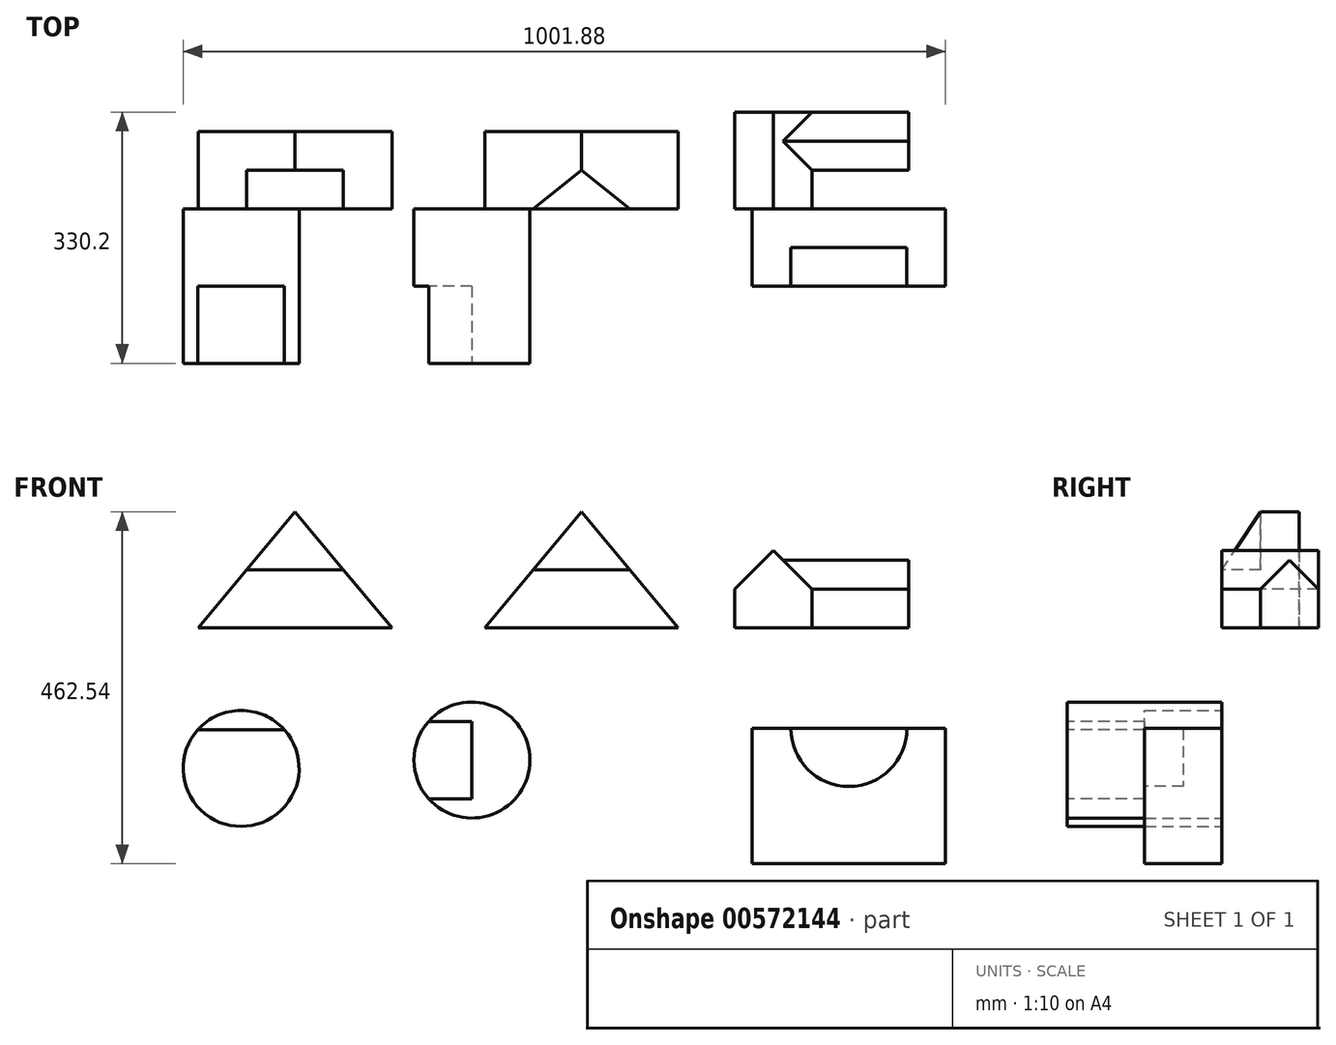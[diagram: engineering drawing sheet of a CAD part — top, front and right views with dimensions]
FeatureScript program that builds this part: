
annotation { "Feature Type Name" : "Feature", "Feature Type Description" : "" }
export const myFeature = defineFeature(function(context is Context, id is Id, definition is map)
    precondition{}
    {
        {
            var Q0;
            Q0=qCreatedBy(makeId("Front.planeOp"),FACE);
            var sketch = newSketch(context, id + "F0", { "sketchPlane" : qUnion([Q0])});
            skLineSegment(sketch, "E0.bottom", {"start": v(148.7, 0) * mm, "end": v(403.3, 0) * mm});
            skLineSegment(sketch, "E1", {"start": v(276, 152.77) * mm, "end": v(403.3, 0) * mm});
            skLineSegment(sketch, "E2", {"start": v(148.7, 0) * mm, "end": v(276, 152.77) * mm});
            skLineSegment(sketch, "E3", {"start": v(212.34, 76.38) * mm, "end": v(339.65, 76.38) * mm});
            skLineSegment(sketch, "E4.bottom", {"start": v(525.25, 0) * mm, "end": v(779.25, 0) * mm});
            skLineSegment(sketch, "E5", {"start": v(525.25, 0) * mm, "end": v(652.25, 152.4) * mm});
            skLineSegment(sketch, "E6", {"start": v(652.25, 152.4) * mm, "end": v(779.25, 0) * mm});
            skLineSegment(sketch, "E7", {"start": v(588.75, 76.2) * mm, "end": v(715.75, 76.2) * mm});
            skSolve(sketch);
        }
        {
            var Q0;
            {var subQ3=sQuery(id+"F0.wireOp",EDGE,"E3");Q0=makeQuery(id+"F0.imprint","IMPRINT",FACE,{"disambiguationData":[TD([[makeQuery(id+"F0.imprint","IMPRINT",EDGE,{"derivedFrom":subQ3}),1.0]])]});}
            var Q1;
            {var subQ0=sQuery(id+"F0.wireOp",EDGE,"E0.bottom");Q1=makeQuery(id+"F0.imprint","IMPRINT",FACE,{"disambiguationData":[TD([[makeQuery(id+"F0.imprint","IMPRINT",EDGE,{"derivedFrom":subQ0}),1.0]])]});}
            extrude(context, id + "F1", {"entities" : qUnion([Q0, Q1]), "oppositeDirection" : true, "depth" : 101.6 * mm, "offsetDistance" : 25.4 * mm});
        }
        {
            var Q0;
            {var subQ3=sQuery(id+"F0.wireOp",EDGE,"E3");Q0=makeQuery(id+"F0.imprint","IMPRINT",FACE,{"disambiguationData":[TD([[makeQuery(id+"F0.imprint","IMPRINT",EDGE,{"derivedFrom":subQ3}),1.0]])]});}
            extrude(context, id + "F2", {"entities" : qUnion([Q0]), "operationType" : NewBodyOperationType.REMOVE, "oppositeDirection" : true, "depth" : 50.8 * mm, "offsetDistance" : 25.4 * mm});
        }
        {
            var Q0;
            {var subQ3=sQuery(id+"F0.wireOp",EDGE,"E7");Q0=makeQuery(id+"F0.imprint","IMPRINT",FACE,{"disambiguationData":[TD([[makeQuery(id+"F0.imprint","IMPRINT",EDGE,{"derivedFrom":subQ3}),1.0]])]});}
            var Q1;
            {var subQ0=sQuery(id+"F0.wireOp",EDGE,"E4.bottom");Q1=makeQuery(id+"F0.imprint","IMPRINT",FACE,{"disambiguationData":[TD([[makeQuery(id+"F0.imprint","IMPRINT",EDGE,{"derivedFrom":subQ0}),1.0]])]});}
            extrude(context, id + "F3", {"entities" : qUnion([Q0, Q1]), "oppositeDirection" : true, "depth" : 101.6 * mm, "offsetDistance" : 25.4 * mm});
        }
        {
            var Q0;
            Q0=makeQuery(id+"F3.opExtrude","CAP_EDGE",EDGE,{"disambiguationData":[OSD([sQuery(id+"F0.wireOp",EDGE,"E4.bottom")])],"isStart":true});
            cPoint(context, id + "F4", {"entities" : qUnion([Q0]), "parameter" : 0.5});
        }
        {
            var Q0;
            Q0=makeQuery(id+"F3.opExtrude","CAP_VERTEX",VERTEX,{"disambiguationData":[OSD([sQuery(id+"F0.wireOp",EDGE,"E5"),sQuery(id+"F0.wireOp",EDGE,"E6")])],"isStart":true});
            var Q1;
            Q1=makeQuery(id+"F3.opExtrude","CAP_VERTEX",VERTEX,{"disambiguationData":[OSD([sQuery(id+"F0.wireOp",EDGE,"E5"),sQuery(id+"F0.wireOp",EDGE,"E6")])],"isStart":false});
            var Q2;
            Q2 = qCreatedBy(id + "F4" ,VERTEX);
            cPlane(context, id + "F5", {"entities" : qUnion([Q0, Q1, Q2]), "cplaneType" : CPlaneType.THREE_POINT, "offset" : 25.4 * mm, "width" : 152.4 * mm, "height" : 152.4 * mm});
        }
        {
            var Q0;
            Q0=qCreatedBy(id+"F5.planeOp",FACE);
            var sketch = newSketch(context, id + "F6", { "sketchPlane" : qUnion([Q0])});
            skLineSegment(sketch, "E8", {"start": v(0, 76.2) * mm, "end": v(50.8, 152.4) * mm});
            skLineSegment(sketch, "E9", {"start": v(50.8, 152.4) * mm, "end": v(0, 152.4) * mm});
            skLineSegment(sketch, "E10", {"start": v(0, 152.4) * mm, "end": v(0, 76.2) * mm});
            skLineSegment(sketch, "E11", {"start": v(0, 0) * mm, "end": v(0, 76.2) * mm});
            skSolve(sketch);
        }
        {
            var Q0;
            Q0 = qSketchRegion(id + "F6", true);
            extrude(context, id + "F7", {"entities" : qUnion([Q0]), "operationType" : NewBodyOperationType.REMOVE, "endBound" : BoundingType.SYMMETRIC, "depth" : 127 * mm, "offsetDistance" : 25.4 * mm});
        }
        {
            var Q0;
            Q0=qCreatedBy(makeId("Front.planeOp"),FACE);
            var sketch = newSketch(context, id + "F8", { "sketchPlane" : qUnion([Q0])});
            skLineSegment(sketch, "E12.bottom", {"start": v(853.5, 0) * mm, "end": v(955.1, 0) * mm});
            skLineSegment(sketch, "E13", {"start": v(853.5, 50.8) * mm, "end": v(904.3, 101.6) * mm});
            skLineSegment(sketch, "E14", {"start": v(904.3, 101.6) * mm, "end": v(955.1, 50.8) * mm});
            skLineSegment(sketch, "E15", {"start": v(853.5, 50.8) * mm, "end": v(853.5, 0) * mm});
            skLineSegment(sketch, "E16", {"start": v(955.1, 0) * mm, "end": v(955.1, 50.8) * mm});
            skSolve(sketch);
        }
        {
            var Q0;
            Q0=makeQuery(id+"F8.imprint","IMPRINT",FACE,{"disambiguationData":[TD([[makeQuery(id+"F8.imprint","IMPRINT",EDGE,{"derivedFrom":sQuery(id+"F8.wireOp",EDGE,"E12.bottom")}),1.0]])]});
            extrude(context, id + "F9", {"entities" : qUnion([Q0]), "oppositeDirection" : true, "depth" : 127 * mm, "offsetDistance" : 25.4 * mm});
        }
        {
            var Q0;
            Q0=makeQuery(id+"F9.opExtrude","SWEPT_FACE",FACE,{"disambiguationData":[OSD([sQuery(id+"F8.wireOp",EDGE,"E16")])]});
            cPlane(context, id + "F10", {"entities" : qUnion([Q0]), "cplaneType" : CPlaneType.OFFSET, "offset" : 127 * mm, "width" : 152.4 * mm, "height" : 152.4 * mm});
        }
        {
            var Q0;
            Q0=qCreatedBy(id+"F10.planeOp",FACE);
            var sketch = newSketch(context, id + "F11", { "sketchPlane" : qUnion([Q0])});
            skLineSegment(sketch, "E17.bottom", {"start": v(127, 0) * mm, "end": v(50.8, 0) * mm});
            skLineSegment(sketch, "E18", {"start": v(50.8, 0) * mm, "end": v(50.8, 50.8) * mm});
            skLineSegment(sketch, "E19", {"start": v(50.8, 50.8) * mm, "end": v(88.9, 88.9) * mm});
            skLineSegment(sketch, "E20", {"start": v(88.9, 88.9) * mm, "end": v(127, 50.8) * mm});
            skLineSegment(sketch, "E21", {"start": v(127, 0) * mm, "end": v(127, 50.8) * mm});
            skSolve(sketch);
        }
        {
            var Q0;
            Q0 = qSketchRegion(id + "F11", true);
            extrude(context, id + "F12", {"entities" : qUnion([Q0]), "operationType" : NewBodyOperationType.ADD, "oppositeDirection" : true, "depth" : 165.1 * mm, "offsetDistance" : 25.4 * mm});
        }
        {
            var Q0;
            Q0=qCreatedBy(makeId("Front.planeOp"),FACE);
            var sketch = newSketch(context, id + "F13", { "sketchPlane" : qUnion([Q0])});
            skCircle(sketch, "E22", {"center": v(205.21, -184.5) * mm, "radius": 76.2 * mm});
            skSolve(sketch);
        }
        {
            var Q0;
            Q0 = qSketchRegion(id + "F13", true);
            extrude(context, id + "F14", {"entities" : qUnion([Q0]), "depth" : 203.2 * mm, "offsetDistance" : 25.4 * mm});
        }
        {
            var Q0;
            Q0=makeQuery(id+"F14.opExtrude","CAP_FACE",FACE,{"disambiguationData":[OSD([sQuery(id+"F13.wireOp",EDGE,"E22")])],"isStart":false});
            var sketch = newSketch(context, id + "F15", { "sketchPlane" : qUnion([Q0])});
            skLineSegment(sketch, "E23", {"start": v(202.75, -133.67) * mm, "end": v(148.45, -133.67) * mm});
            skLineSegment(sketch, "E24", {"start": v(148.45, -133.67) * mm, "end": v(261.97, -133.67) * mm});
            skSolve(sketch);
        }
        {
            var Q0;
            {var subQ0=sQuery(id+"F15.wireOp",EDGE,"E24");var subQ3=makeQuery(id+"F15.imprint","IMPRINT",VERTEX,{"derivedFrom":subQ0});Q0=makeQuery(id+"F15.imprint","IMPRINT",FACE,{"disambiguationData":[TD([[makeQuery(id+"F15.imprint","IMPRINT",EDGE,{"disambiguationData":[TD([[subQ3,1.0]])],"derivedFrom":subQ0}),1.0]])]});}
            extrude(context, id + "F16", {"entities" : qUnion([Q0]), "operationType" : NewBodyOperationType.REMOVE, "oppositeDirection" : true, "depth" : 101.6 * mm, "offsetDistance" : 25.4 * mm});
        }
        {
            var Q0;
            Q0=qCreatedBy(makeId("Front.planeOp"),FACE);
            var sketch = newSketch(context, id + "F17", { "sketchPlane" : qUnion([Q0])});
            skCircle(sketch, "E25", {"center": v(508.52, -173.49) * mm, "radius": 76.2 * mm});
            skLineSegment(sketch, "E26", {"start": v(508.52, -224.29) * mm, "end": v(451.72, -224.29) * mm});
            skLineSegment(sketch, "E27", {"start": v(508.52, -122.69) * mm, "end": v(451.72, -122.69) * mm});
            skLineSegment(sketch, "E28", {"start": v(508.52, -122.69) * mm, "end": v(508.52, -224.29) * mm});
            skSolve(sketch);
        }
        {
            var Q0;
            {var subQ0=sQuery(id+"F17.wireOp",EDGE,"E26");Q0=makeQuery(id+"F17.imprint","IMPRINT",FACE,{"disambiguationData":[TD([[makeQuery(id+"F17.imprint","IMPRINT",EDGE,{"derivedFrom":subQ0}),1.0]])]});}
            var Q1;
            {var subQ0=sQuery(id+"F17.wireOp",EDGE,"E26");Q1=makeQuery(id+"F17.imprint","IMPRINT",FACE,{"disambiguationData":[TD([[makeQuery(id+"F17.imprint","IMPRINT",EDGE,{"derivedFrom":subQ0}),-1.0]])]});}
            extrude(context, id + "F18", {"entities" : qUnion([Q0, Q1]), "depth" : 203.2 * mm, "offsetDistance" : 25.4 * mm});
        }
        {
            var Q0;
            Q0=makeQuery(id+"F18.opExtrude","CAP_FACE",FACE,{"disambiguationData":[OSD([sQuery(id+"F17.wireOp",EDGE,"E25")])],"isStart":false});
            var sketch = newSketch(context, id + "F19", { "sketchPlane" : qUnion([Q0])});
            skLineSegment(sketch, "E29", {"start": v(508.52, -122.69) * mm, "end": v(451.72, -122.69) * mm});
            skLineSegment(sketch, "E30", {"start": v(508.52, -224.29) * mm, "end": v(451.72, -224.29) * mm});
            skLineSegment(sketch, "E31", {"start": v(508.52, -122.69) * mm, "end": v(508.52, -224.29) * mm});
            skSolve(sketch);
        }
        {
            var Q0;
            {var subQ0=sQuery(id+"F19.wireOp",EDGE,"E29");Q0=makeQuery(id+"F19.imprint","IMPRINT",FACE,{"disambiguationData":[TD([[makeQuery(id+"F19.imprint","IMPRINT",EDGE,{"derivedFrom":subQ0}),1.0]])]});}
            extrude(context, id + "F20", {"entities" : qUnion([Q0]), "operationType" : NewBodyOperationType.REMOVE, "oppositeDirection" : true, "depth" : 101.6 * mm, "offsetDistance" : 25.4 * mm});
        }
        {
            var Q0;
            Q0=qCreatedBy(makeId("Front.planeOp"),FACE);
            var sketch = newSketch(context, id + "F21", { "sketchPlane" : qUnion([Q0])});
            skLineSegment(sketch, "E32.bottom", {"start": v(876.9, -131.97) * mm, "end": v(1130.9, -131.97) * mm});
            skLineSegment(sketch, "E32.top", {"start": v(876.9, -309.77) * mm, "end": v(1130.9, -309.77) * mm});
            skLineSegment(sketch, "E32.left", {"start": v(876.9, -131.97) * mm, "end": v(876.9, -309.77) * mm});
            skLineSegment(sketch, "E32.right", {"start": v(1130.9, -131.97) * mm, "end": v(1130.9, -309.77) * mm});
            skSolve(sketch);
        }
        {
            var Q0;
            Q0 = qSketchRegion(id + "F21", true);
            extrude(context, id + "F22", {"entities" : qUnion([Q0]), "depth" : 101.6 * mm, "offsetDistance" : 25.4 * mm});
        }
        {
            var Q0;
            Q0=makeQuery(id+"F22.opExtrude","CAP_FACE",FACE,{"disambiguationData":[OSD([sQuery(id+"F21.wireOp",EDGE,"E32.bottom"),sQuery(id+"F21.wireOp",EDGE,"E32.top"),sQuery(id+"F21.wireOp",EDGE,"E32.left"),sQuery(id+"F21.wireOp",EDGE,"E32.right")])],"isStart":false});
            var sketch = newSketch(context, id + "F23", { "sketchPlane" : qUnion([Q0])});
            skLineSegment(sketch, "E33", {"start": v(876.9, -131.97) * mm, "end": v(927.7, -131.97) * mm});
            skLineSegment(sketch, "E34", {"start": v(1130.9, -131.97) * mm, "end": v(1080.1, -131.97) * mm});
            skCircle(sketch, "E35", {"center": v(1003.9, -131.97) * mm, "radius": 76.2 * mm});
            skSolve(sketch);
        }
        {
            var Q0;
            {var subQ0=sQuery(id+"F23.wireOp",EDGE,"E35");var subQ1=makeQuery(id+"F22.opExtrude","CAP_EDGE",EDGE,{"disambiguationData":[OSD([sQuery(id+"F21.wireOp",EDGE,"E32.bottom")])],"isStart":false});var subQ2=makeQuery(id+"F23.imprint","INTERSECT",VERTEX,{"derivedFrom":[subQ1,sQuery(id+"F23.wireOp",EDGE,"E33"),subQ0]});Q0=makeQuery(id+"F23.imprint","IMPRINT",FACE,{"disambiguationData":[TD([[makeQuery(id+"F23.imprint","IMPRINT",EDGE,{"disambiguationData":[TD([[subQ2,-1.0]])],"derivedFrom":subQ0}),1.0]])]});}
            extrude(context, id + "F24", {"entities" : qUnion([Q0]), "operationType" : NewBodyOperationType.REMOVE, "oppositeDirection" : true, "depth" : 50.8 * mm, "offsetDistance" : 25.4 * mm});
        }
    });
